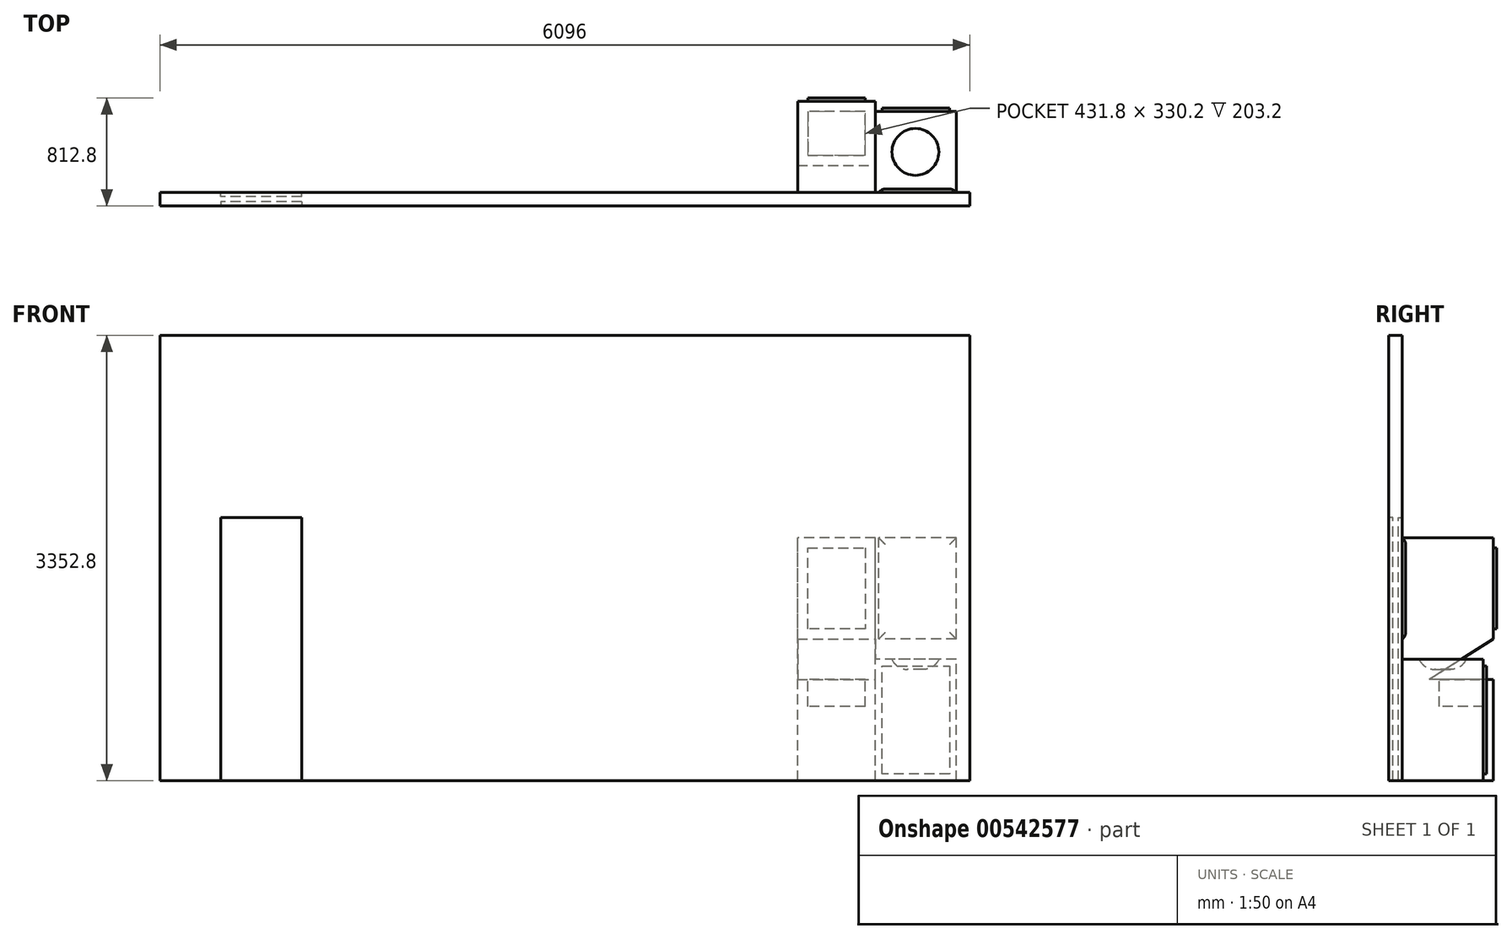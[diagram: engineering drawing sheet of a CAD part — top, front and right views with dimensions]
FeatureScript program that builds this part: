
annotation { "Feature Type Name" : "Feature", "Feature Type Description" : "" }
export const myFeature = defineFeature(function(context is Context, id is Id, definition is map)
    precondition{}
    {
        {
            var Q0;
            Q0=qCreatedBy(makeId("Front.planeOp"),FACE);
            var sketch = newSketch(context, id + "F0", { "sketchPlane" : qUnion([Q0])});
            skLineSegment(sketch, "E0.bottom", {"start": v(0, 0) * mm, "end": v(-6096, 0) * mm});
            skLineSegment(sketch, "E0.top", {"start": v(0, 3352.8) * mm, "end": v(-6096, 3352.8) * mm});
            skLineSegment(sketch, "E0.left", {"start": v(0, 0) * mm, "end": v(0, 3352.8) * mm});
            skLineSegment(sketch, "E0.right", {"start": v(-6096, 0) * mm, "end": v(-6096, 3352.8) * mm});
            skSolve(sketch);
        }
        {
            var Q0;
            Q0=makeQuery(id+"F0.imprint","IMPRINT",FACE,{"disambiguationData":[TD([[makeQuery(id+"F0.imprint","IMPRINT",EDGE,{"derivedFrom":sQuery(id+"F0.wireOp",EDGE,"E0.bottom")}),-1.0]])]});
            extrude(context, id + "F1", {"entities" : qUnion([Q0]), "depth" : 101.6 * mm, "offsetDistance" : 30.48 * mm});
        }
        {
            var Q0;
            Q0=makeQuery(id+"F1.opExtrude","CAP_FACE",FACE,{"disambiguationData":[OSD([sQuery(id+"F0.wireOp",EDGE,"E0.bottom"),sQuery(id+"F0.wireOp",EDGE,"E0.top"),sQuery(id+"F0.wireOp",EDGE,"E0.left"),sQuery(id+"F0.wireOp",EDGE,"E0.right")])],"isStart":false});
            var sketch = newSketch(context, id + "F2", { "sketchPlane" : qUnion([Q0])});
            skLineSegment(sketch, "E1.bottom", {"start": v(-6096, 0) * mm, "end": v(-5638.8, 0) * mm, "construction": true});
            skLineSegment(sketch, "E1.top", {"start": v(-6096, 609.6) * mm, "end": v(-5638.8, 609.6) * mm, "construction": true});
            skLineSegment(sketch, "E1.left", {"start": v(-6096, 0) * mm, "end": v(-6096, 609.6) * mm, "construction": true});
            skLineSegment(sketch, "E1.right", {"start": v(-5638.8, 0) * mm, "end": v(-5638.8, 609.6) * mm, "construction": true});
            skLineSegment(sketch, "E2.bottom", {"start": v(-5638.8, 0) * mm, "end": v(-5029.2, 0) * mm});
            skLineSegment(sketch, "E2.top", {"start": v(-5638.8, 1981.2) * mm, "end": v(-5029.2, 1981.2) * mm});
            skLineSegment(sketch, "E2.left", {"start": v(-5638.8, 0) * mm, "end": v(-5638.8, 1981.2) * mm});
            skLineSegment(sketch, "E2.right", {"start": v(-5029.2, 0) * mm, "end": v(-5029.2, 1981.2) * mm});
            skSolve(sketch);
        }
        {
            var Q0;
            Q0=makeQuery(id+"F2.imprint","IMPRINT",FACE,{"disambiguationData":[TD([[makeQuery(id+"F2.imprint","IMPRINT",EDGE,{"derivedFrom":sQuery(id+"F2.wireOp",EDGE,"E2.bottom")}),-1.0]])]});
            extrude(context, id + "F3", {"entities" : qUnion([Q0]), "operationType" : NewBodyOperationType.REMOVE, "oppositeDirection" : true, "depth" : 30.48 * mm, "offsetDistance" : 30.48 * mm});
        }
        {
            var Q0;
            Q0=makeQuery(id+"F1.opExtrude","CAP_FACE",FACE,{"disambiguationData":[OSD([sQuery(id+"F0.wireOp",EDGE,"E0.bottom"),sQuery(id+"F0.wireOp",EDGE,"E0.top"),sQuery(id+"F0.wireOp",EDGE,"E0.left"),sQuery(id+"F0.wireOp",EDGE,"E0.right")])],"isStart":true});
            var sketch = newSketch(context, id + "F4", { "sketchPlane" : qUnion([Q0])});
            skLineSegment(sketch, "E3", {"start": v(6096, 0) * mm, "end": v(5638.8, 0) * mm});
            skLineSegment(sketch, "E4.bottom", {"start": v(5638.8, 0) * mm, "end": v(5029.2, 0) * mm});
            skLineSegment(sketch, "E4.top", {"start": v(5638.8, 1981.2) * mm, "end": v(5029.2, 1981.2) * mm});
            skLineSegment(sketch, "E4.left", {"start": v(5638.8, 0) * mm, "end": v(5638.8, 1981.2) * mm});
            skLineSegment(sketch, "E4.right", {"start": v(5029.2, 0) * mm, "end": v(5029.2, 1981.2) * mm});
            skSolve(sketch);
        }
        {
            var Q0;
            Q0=makeQuery(id+"F4.imprint","IMPRINT",FACE,{"disambiguationData":[TD([[makeQuery(id+"F4.imprint","IMPRINT",EDGE,{"derivedFrom":sQuery(id+"F4.wireOp",EDGE,"E4.bottom")}),1.0]])]});
            extrude(context, id + "F5", {"entities" : qUnion([Q0]), "operationType" : NewBodyOperationType.REMOVE, "oppositeDirection" : true, "depth" : 30.48 * mm, "offsetDistance" : 30.48 * mm});
        }
        {
            var Q0;
            Q0=makeQuery(id+"F1.opExtrude","CAP_FACE",FACE,{"disambiguationData":[OSD([sQuery(id+"F0.wireOp",EDGE,"E0.bottom"),sQuery(id+"F0.wireOp",EDGE,"E0.top"),sQuery(id+"F0.wireOp",EDGE,"E0.left"),sQuery(id+"F0.wireOp",EDGE,"E0.right")])],"isStart":true});
            var sketch = newSketch(context, id + "F6", { "sketchPlane" : qUnion([Q0])});
            skLineSegment(sketch, "E5.bottom", {"start": v(101.6, 0) * mm, "end": v(711.2, 0) * mm});
            skLineSegment(sketch, "E5.top", {"start": v(101.6, 914.4) * mm, "end": v(711.2, 914.4) * mm});
            skLineSegment(sketch, "E5.left", {"start": v(101.6, 0) * mm, "end": v(101.6, 914.4) * mm});
            skLineSegment(sketch, "E5.right", {"start": v(711.2, 0) * mm, "end": v(711.2, 914.4) * mm});
            skLineSegment(sketch, "E6.bottom", {"start": v(711.2, 0) * mm, "end": v(1295.4, 0) * mm});
            skLineSegment(sketch, "E6.top", {"start": v(711.2, 1828.8) * mm, "end": v(1295.4, 1828.8) * mm});
            skLineSegment(sketch, "E6.left", {"start": v(711.2, 0) * mm, "end": v(711.2, 1828.8) * mm});
            skLineSegment(sketch, "E6.right", {"start": v(1295.4, 0) * mm, "end": v(1295.4, 1828.8) * mm});
            skLineSegment(sketch, "E7.bottom", {"start": v(101.6, 1066.8) * mm, "end": v(685.8, 1066.8) * mm});
            skLineSegment(sketch, "E7.top", {"start": v(101.6, 1828.8) * mm, "end": v(685.8, 1828.8) * mm});
            skLineSegment(sketch, "E7.left", {"start": v(101.6, 1066.8) * mm, "end": v(101.6, 1828.8) * mm});
            skLineSegment(sketch, "E7.right", {"start": v(685.8, 1066.8) * mm, "end": v(685.8, 1828.8) * mm});
            skSolve(sketch);
        }
        {
            var Q0;
            {var subQ3=sQuery(id+"F6.wireOp",EDGE,"E6.bottom");Q0=makeQuery(id+"F6.imprint","IMPRINT",FACE,{"disambiguationData":[TD([[makeQuery(id+"F6.imprint","IMPRINT",EDGE,{"derivedFrom":subQ3}),1.0]])]});}
            extrude(context, id + "F7", {"entities" : qUnion([Q0]), "operationType" : NewBodyOperationType.ADD, "depth" : 685.8 * mm, "offsetDistance" : 25.4 * mm});
        }
        {
            var Q0;
            Q0=makeQuery(id+"F7.opExtrude","SWEPT_FACE",FACE,{"disambiguationData":[OSD([sQuery(id+"F6.wireOp",EDGE,"E6.left")])]});
            var sketch = newSketch(context, id + "F8", { "sketchPlane" : qUnion([Q0])});
            skLineSegment(sketch, "E8.bottom", {"start": v(685.8, 0) * mm, "end": v(203.2, 0) * mm});
            skLineSegment(sketch, "E8.top", {"start": v(685.8, 762) * mm, "end": v(203.2, 762) * mm});
            skLineSegment(sketch, "E8.left", {"start": v(685.8, 0) * mm, "end": v(685.8, 762) * mm});
            skLineSegment(sketch, "E8.right", {"start": v(203.2, 0) * mm, "end": v(203.2, 762) * mm});
            skLineSegment(sketch, "E9", {"start": v(685.8, 1828.8) * mm, "end": v(685.8, 1066.8) * mm});
            skLineSegment(sketch, "E10", {"start": v(685.8, 1066.8) * mm, "end": v(203.2, 762) * mm});
            skSolve(sketch);
        }
        {
            var Q0;
            {var subQ0=sQuery(id+"F8.wireOp",EDGE,"E8.top");Q0=makeQuery(id+"F8.imprint","IMPRINT",FACE,{"disambiguationData":[TD([[makeQuery(id+"F8.imprint","IMPRINT",EDGE,{"derivedFrom":subQ0}),-1.0]])]});}
            extrude(context, id + "F9", {"entities" : qUnion([Q0]), "operationType" : NewBodyOperationType.REMOVE, "oppositeDirection" : true, "depth" : 609.6 * mm, "offsetDistance" : 25.4 * mm});
        }
        {
            var Q0;
            {var subQ0=sQuery(id+"F6.wireOp",EDGE,"E5.bottom");Q0=makeQuery(id+"F6.imprint","IMPRINT",FACE,{"disambiguationData":[TD([[makeQuery(id+"F6.imprint","IMPRINT",EDGE,{"derivedFrom":subQ0}),1.0]])]});}
            extrude(context, id + "F10", {"entities" : qUnion([Q0]), "operationType" : NewBodyOperationType.ADD, "depth" : 609.6 * mm, "offsetDistance" : 25.4 * mm});
        }
        {
            var Q0;
            Q0=makeQuery(id+"F10.opExtrude","SWEPT_FACE",FACE,{"disambiguationData":[OSD([sQuery(id+"F6.wireOp",EDGE,"E5.top")])]});
            var sketch = newSketch(context, id + "F11", { "sketchPlane" : qUnion([Q0])});
            skCircle(sketch, "E11", {"center": v(-408.95, 304.8) * mm, "radius": 176.67 * mm});
            skPoint(sketch, "E11.centerSnap0", {"position": v(-101.6, 304.8) * mm});
            skSolve(sketch);
        }
        {
            var Q0;
            Q0=makeQuery(id+"F11.imprint","IMPRINT",FACE,{"disambiguationData":[TD([[makeQuery(id+"F11.imprint","IMPRINT",EDGE,{"derivedFrom":sQuery(id+"F11.wireOp",EDGE,"E11")}),1.0]])]});
            extrude(context, id + "F12", {"entities" : qUnion([Q0]), "operationType" : NewBodyOperationType.REMOVE, "oppositeDirection" : true, "depth" : 76.2 * mm, "offsetDistance" : 25.4 * mm});
        }
        {
            var Q0;
            Q0=makeQuery(id+"F12.boolean.opBoolean","COPY",FACE,{"derivedFrom":makeQuery(id+"F12.opExtrude","CAP_FACE",FACE,{"disambiguationData":[OSD([sQuery(id+"F11.wireOp",EDGE,"E11")])],"isStart":false})});
            fillet(context, id + "F13", {"entities" : qUnion([Q0]), "radius" : 127 * mm, "tangentPropagation" : true, "allowEdgeOverflow" : false});
        }
        {
            var Q0;
            {var subQ0=sQuery(id+"F6.wireOp",EDGE,"E6.top");var subQ1=sQuery(id+"F6.wireOp",EDGE,"E6.left");var subQ2=sQuery(id+"F6.wireOp",EDGE,"E6.right");Q0=makeQuery(id+"F9.boolean.opBoolean","SPLIT",FACE,{"disambiguationData":[TD([makeQuery(id+"F7.opExtrude","SWEPT_FACE",FACE,{"disambiguationData":[OSD([subQ0])]})])],"derivedFrom":makeQuery(id+"F7.opExtrude","CAP_FACE",FACE,{"disambiguationData":[OSD([sQuery(id+"F6.wireOp",EDGE,"E6.bottom"),subQ0,subQ1,subQ2])],"isStart":false})});}
            var sketch = newSketch(context, id + "F14", { "sketchPlane" : qUnion([Q0])});
            skLineSegment(sketch, "E12.0", {"start": v(787.4, 1143) * mm, "end": v(1219.2, 1143) * mm});
            skLineSegment(sketch, "E12.1", {"start": v(787.4, 1752.6) * mm, "end": v(787.4, 1143) * mm});
            skLineSegment(sketch, "E12.2", {"start": v(1219.2, 1752.6) * mm, "end": v(787.4, 1752.6) * mm});
            skLineSegment(sketch, "E12.3", {"start": v(1219.2, 1143) * mm, "end": v(1219.2, 1752.6) * mm});
            skSolve(sketch);
        }
        {
            var Q0;
            Q0=makeQuery(id+"F14.imprint","IMPRINT",FACE,{"disambiguationData":[TD([[makeQuery(id+"F14.imprint","IMPRINT",EDGE,{"derivedFrom":sQuery(id+"F14.wireOp",EDGE,"E12.0")}),1.0]])]});
            extrude(context, id + "F15", {"entities" : qUnion([Q0]), "operationType" : NewBodyOperationType.ADD, "depth" : 25.4 * mm, "offsetDistance" : 25.4 * mm});
        }
        {
            var Q0;
            Q0=makeQuery(id+"F9.boolean.opBoolean","COPY",FACE,{"derivedFrom":makeQuery(id+"F9.opExtrude","SWEPT_FACE",FACE,{"disambiguationData":[OSD([sQuery(id+"F8.wireOp",EDGE,"E8.top")])]})});
            var sketch = newSketch(context, id + "F16", { "sketchPlane" : qUnion([Q0])});
            skLineSegment(sketch, "E13.0", {"start": v(-1219.2, 609.6) * mm, "end": v(-1219.2, 279.4) * mm});
            skLineSegment(sketch, "E13.1", {"start": v(-787.4, 609.6) * mm, "end": v(-1219.2, 609.6) * mm});
            skLineSegment(sketch, "E13.2", {"start": v(-787.4, 279.4) * mm, "end": v(-787.4, 609.6) * mm});
            skLineSegment(sketch, "E13.3", {"start": v(-1219.2, 279.4) * mm, "end": v(-787.4, 279.4) * mm});
            skSolve(sketch);
        }
        {
            var Q0;
            Q0=makeQuery(id+"F16.imprint","IMPRINT",FACE,{"disambiguationData":[TD([[makeQuery(id+"F16.imprint","IMPRINT",EDGE,{"derivedFrom":sQuery(id+"F16.wireOp",EDGE,"E13.0")}),1.0]])]});
            extrude(context, id + "F17", {"entities" : qUnion([Q0]), "operationType" : NewBodyOperationType.REMOVE, "oppositeDirection" : true, "depth" : 203.2 * mm, "offsetDistance" : 25.4 * mm});
        }
        {
            var Q0;
            Q0=makeQuery(id+"F10.opExtrude","CAP_FACE",FACE,{"disambiguationData":[OSD([sQuery(id+"F6.wireOp",EDGE,"E5.bottom"),sQuery(id+"F6.wireOp",EDGE,"E5.top"),sQuery(id+"F6.wireOp",EDGE,"E5.left"),sQuery(id+"F6.wireOp",EDGE,"E6.left")])],"isStart":false});
            var sketch = newSketch(context, id + "F18", { "sketchPlane" : qUnion([Q0])});
            skLineSegment(sketch, "E14.0", {"start": v(660.4, 50.8) * mm, "end": v(660.4, 762) * mm});
            skLineSegment(sketch, "E14.1", {"start": v(152.4, 50.8) * mm, "end": v(660.4, 50.8) * mm});
            skLineSegment(sketch, "E14.2", {"start": v(660.4, 762) * mm, "end": v(660.4, 863.6) * mm});
            skLineSegment(sketch, "E14.3", {"start": v(660.4, 863.6) * mm, "end": v(152.4, 863.6) * mm});
            skLineSegment(sketch, "E14.4", {"start": v(152.4, 863.6) * mm, "end": v(152.4, 50.8) * mm});
            skSolve(sketch);
        }
        {
            var Q0;
            Q0=makeQuery(id+"F18.imprint","IMPRINT",FACE,{"disambiguationData":[TD([[makeQuery(id+"F18.imprint","IMPRINT",EDGE,{"derivedFrom":sQuery(id+"F18.wireOp",EDGE,"E14.0")}),1.0]])]});
            extrude(context, id + "F19", {"entities" : qUnion([Q0]), "operationType" : NewBodyOperationType.ADD, "depth" : 25.4 * mm, "offsetDistance" : 25.4 * mm});
        }
        {
            var Q0;
            Q0=makeQuery(id+"F6.imprint","IMPRINT",FACE,{"disambiguationData":[TD([[makeQuery(id+"F6.imprint","IMPRINT",EDGE,{"derivedFrom":sQuery(id+"F6.wireOp",EDGE,"E7.bottom")}),1.0]])]});
            extrude(context, id + "F20", {"entities" : qUnion([Q0]), "operationType" : NewBodyOperationType.ADD, "depth" : 25.4 * mm, "offsetDistance" : 30.48 * mm});
        }
        {
            var Q0;
            Q0=makeQuery(id+"F20.opExtrude","CAP_FACE",FACE,{"disambiguationData":[OSD([sQuery(id+"F6.wireOp",EDGE,"E7.bottom"),sQuery(id+"F6.wireOp",EDGE,"E7.top"),sQuery(id+"F6.wireOp",EDGE,"E7.left"),sQuery(id+"F6.wireOp",EDGE,"E7.right")])],"isStart":false});
            fillet(context, id + "F21", {"entities" : qUnion([Q0]), "radius" : 60.96 * mm, "tangentPropagation" : true, "allowEdgeOverflow" : false});
        }
    });
